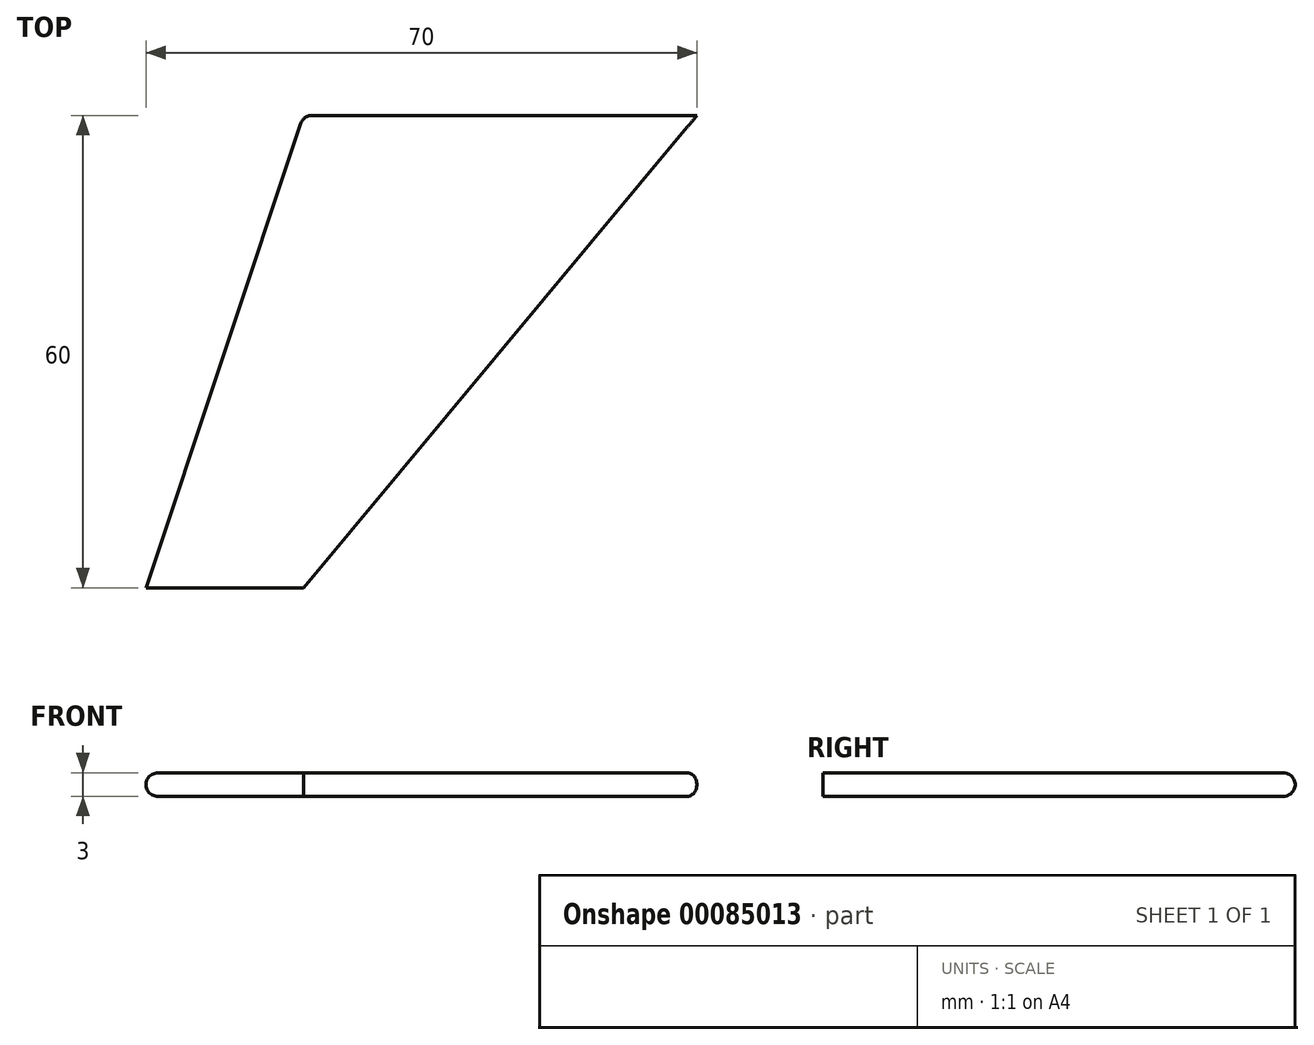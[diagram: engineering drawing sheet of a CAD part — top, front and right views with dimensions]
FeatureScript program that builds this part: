
annotation { "Feature Type Name" : "Feature", "Feature Type Description" : "" }
export const myFeature = defineFeature(function(context is Context, id is Id, definition is map)
    precondition{}
    {
        {
            var Q0;
            Q0=qCreatedBy(makeId("Top.planeOp"),FACE);
            var sketch = newSketch(context, id + "F0", { "sketchPlane" : qUnion([Q0])});
            skLineSegment(sketch, "E0", {"start": v(0, 0) * mm, "end": v(20, 0) * mm});
            skLineSegment(sketch, "E1", {"start": v(20, 0) * mm, "end": v(70, 60) * mm});
            skLineSegment(sketch, "E2", {"start": v(70, 60) * mm, "end": v(20, 60) * mm});
            skLineSegment(sketch, "E3", {"start": v(20, 60) * mm, "end": v(0, 0) * mm});
            skSolve(sketch);
        }
        {
            var Q0;
            Q0=makeQuery(id+"F0.imprint","IMPRINT",FACE,{"disambiguationData":[TD([[makeQuery(id+"F0.imprint","IMPRINT",EDGE,{"derivedFrom":sQuery(id+"F0.wireOp",EDGE,"E0")}),1.0]])]});
            extrude(context, id + "F1", {"entities" : qUnion([Q0]), "depth" : 3 * mm});
        }
        {
            var Q0;
            Q0=makeQuery(id+"F1.opExtrude","CAP_EDGE",EDGE,{"disambiguationData":[OSD([sQuery(id+"F0.wireOp",EDGE,"E2")])],"isStart":false});
            var Q1;
            Q1=makeQuery(id+"F1.opExtrude","CAP_EDGE",EDGE,{"disambiguationData":[OSD([sQuery(id+"F0.wireOp",EDGE,"E3")])],"isStart":true});
            var Q2;
            Q2=makeQuery(id+"F1.opExtrude","CAP_EDGE",EDGE,{"disambiguationData":[OSD([sQuery(id+"F0.wireOp",EDGE,"E3")])],"isStart":false});
            var Q3;
            Q3=makeQuery(id+"F1.opExtrude","CAP_EDGE",EDGE,{"disambiguationData":[OSD([sQuery(id+"F0.wireOp",EDGE,"E2")])],"isStart":true});
            var Q4;
            Q4=makeQuery(id+"F1.opExtrude","SWEPT_EDGE",EDGE,{"disambiguationData":[OSD([sQuery(id+"F0.wireOp",EDGE,"E2"),sQuery(id+"F0.wireOp",EDGE,"E3")])]});
            fillet(context, id + "F2", {"entities" : qUnion([Q0, Q1, Q2, Q3, Q4]), "radius" : 1.5 * mm, "tangentPropagation" : true, "allowEdgeOverflow" : false});
        }
    });
